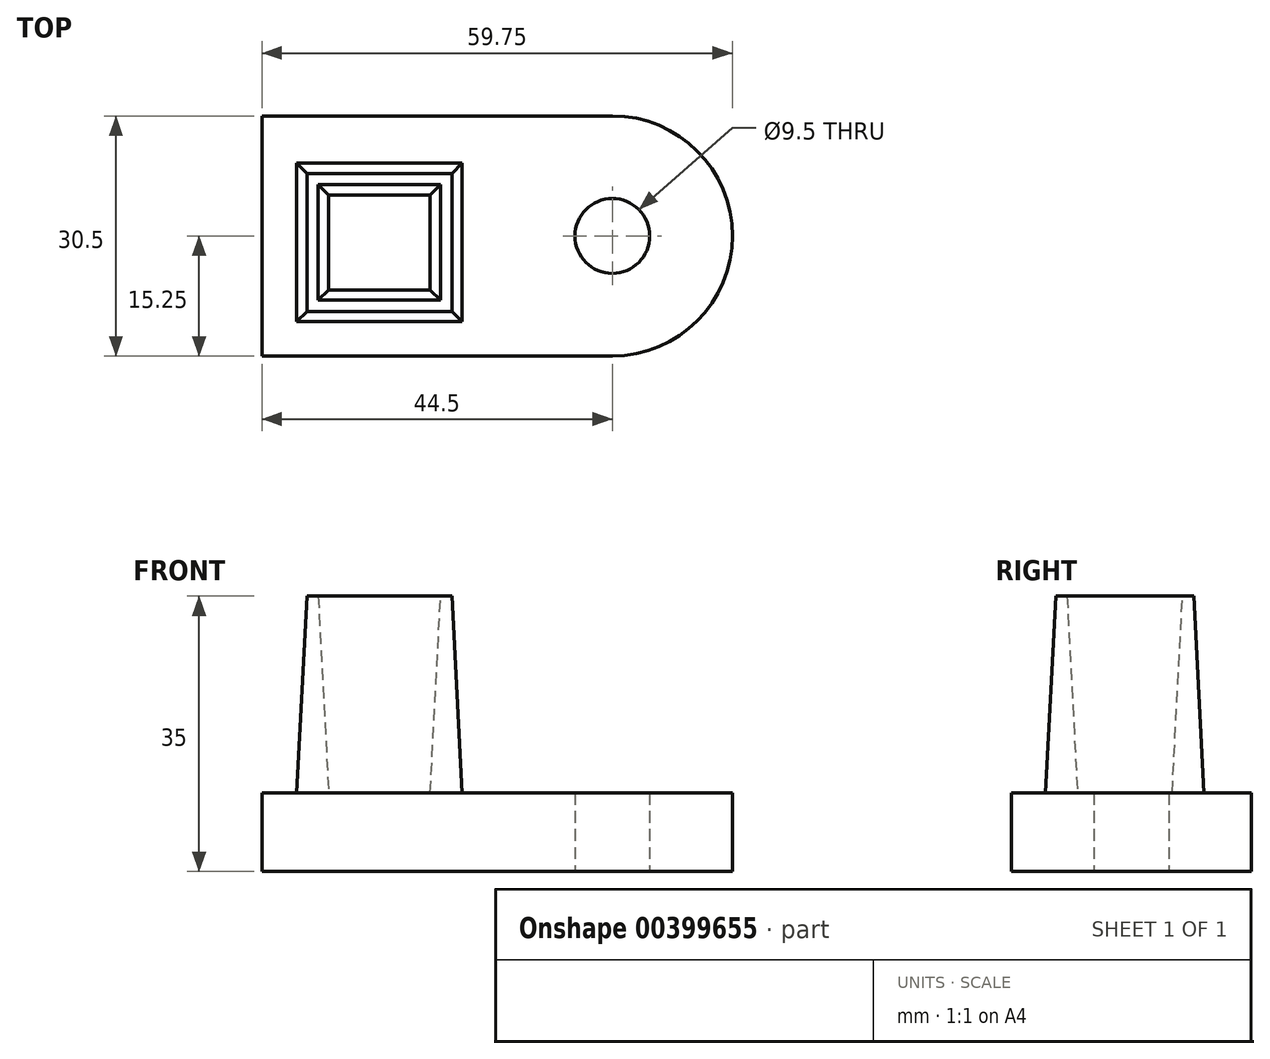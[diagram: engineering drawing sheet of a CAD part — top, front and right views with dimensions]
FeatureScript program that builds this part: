
annotation { "Feature Type Name" : "Feature", "Feature Type Description" : "" }
export const myFeature = defineFeature(function(context is Context, id is Id, definition is map)
    precondition{}
    {
        {
            var Q0;
            Q0=qCreatedBy(makeId("Top.planeOp"),FACE);
            var sketch = newSketch(context, id + "F0", { "sketchPlane" : qUnion([Q0])});
            skLineSegment(sketch, "E0.bottom", {"start": v(-22.25, 15.25) * mm, "end": v(22.25, 15.25) * mm});
            skLineSegment(sketch, "E0.top", {"start": v(-22.25, -15.25) * mm, "end": v(22.25, -15.25) * mm});
            skLineSegment(sketch, "E0.left", {"start": v(-22.25, 15.25) * mm, "end": v(-22.25, -15.25) * mm});
            skLineSegment(sketch, "E0.right", {"start": v(22.25, 15.25) * mm, "end": v(22.25, -15.25) * mm, "construction": true});
            skPoint(sketch, "E0.middle", {"position": v(0, 0) * mm});
            skCircle(sketch, "E1", {"center": v(22.25, 0) * mm, "radius": 4.75 * mm});
            skCircle(sketch, "E2", {"center": v(22.25, 0) * mm, "radius": 15.25 * mm});
            skSolve(sketch);
        }
        {
            var Q0;
            Q0 = qSketchRegion(id + "F0", true);
            extrude(context, id + "F1", {"entities" : qUnion([Q0]), "depth" : 10 * mm});
        }
        {
            var Q0;
            Q0=makeQuery(id+"F1.opExtrude","CAP_FACE",FACE,{"disambiguationData":[OSD([sQuery(id+"F0.wireOp",EDGE,"E0.bottom"),sQuery(id+"F0.wireOp",EDGE,"E0.top"),sQuery(id+"F0.wireOp",EDGE,"E0.left"),sQuery(id+"F0.wireOp",EDGE,"E1"),sQuery(id+"F0.wireOp",EDGE,"E2")])],"isStart":false});
            var sketch = newSketch(context, id + "F2", { "sketchPlane" : qUnion([Q0])});
            skPoint(sketch, "E3.middle", {"position": v(0, 0) * mm});
            skLineSegment(sketch, "E4.bottom", {"start": v(-17.85, 9.25) * mm, "end": v(3.18, 9.25) * mm});
            skLineSegment(sketch, "E4.top", {"start": v(-17.85, -10.9) * mm, "end": v(3.18, -10.9) * mm});
            skLineSegment(sketch, "E4.left", {"start": v(-17.85, 9.25) * mm, "end": v(-17.85, -10.9) * mm});
            skLineSegment(sketch, "E4.right", {"start": v(3.18, 9.25) * mm, "end": v(3.18, -10.9) * mm});
            skLineSegment(sketch, "E5.0", {"start": v(-13.8, -6.84) * mm, "end": v(-0.88, -6.84) * mm});
            skLineSegment(sketch, "E5.1", {"start": v(-13.8, 5.2) * mm, "end": v(-13.8, -6.84) * mm});
            skLineSegment(sketch, "E5.2", {"start": v(-13.8, 5.2) * mm, "end": v(-0.88, 5.2) * mm});
            skLineSegment(sketch, "E5.3", {"start": v(-0.88, 5.2) * mm, "end": v(-0.88, -6.84) * mm});
            skSolve(sketch);
        }
        {
            var Q0;
            Q0=makeQuery(id+"F2.imprint","IMPRINT",FACE,{"disambiguationData":[TD([[makeQuery(id+"F2.imprint","IMPRINT",EDGE,{"derivedFrom":sQuery(id+"F2.wireOp",EDGE,"E4.bottom")}),-1.0]])]});
            extrude(context, id + "F3", {"entities" : qUnion([Q0]), "operationType" : NewBodyOperationType.ADD, "depth" : 25 * mm, "hasDraft" : true, "draftAngle" : 3 * degree, "draftPullDirection" : true});
        }
    });
